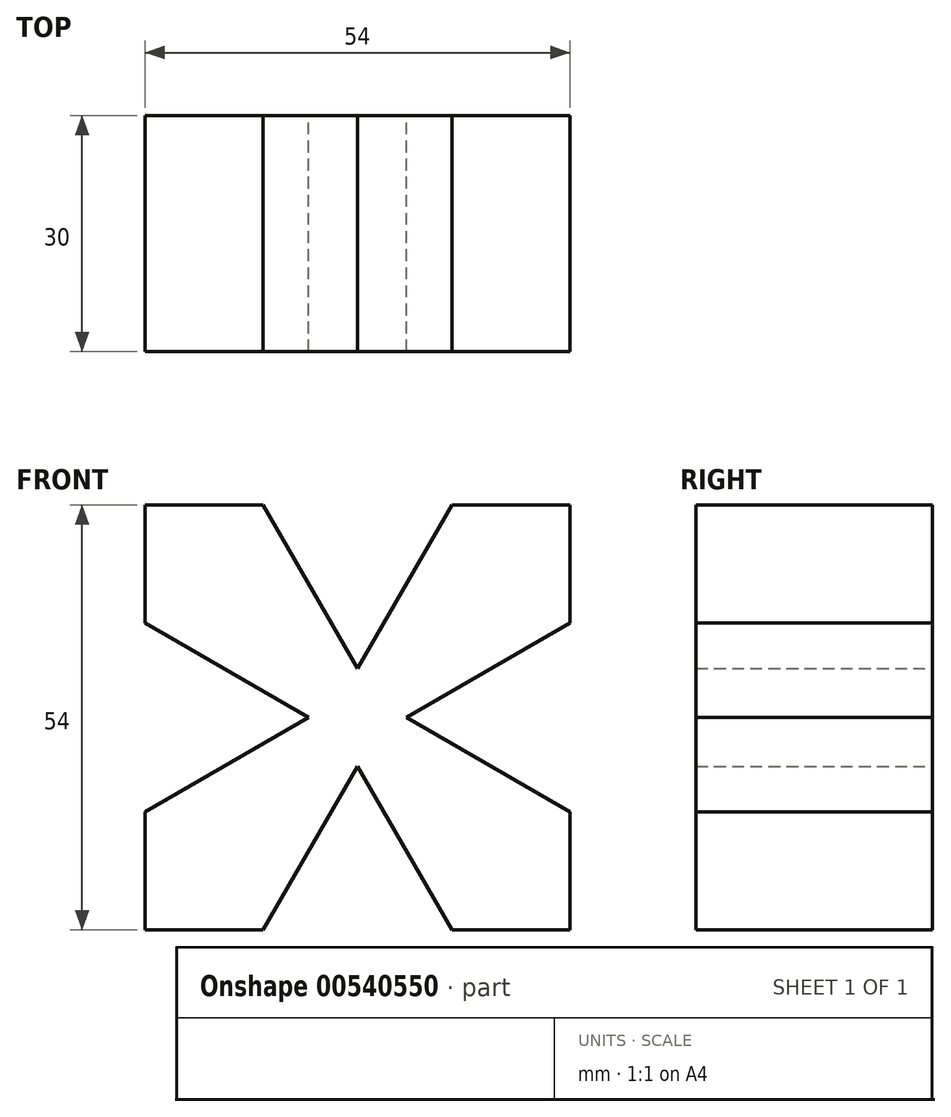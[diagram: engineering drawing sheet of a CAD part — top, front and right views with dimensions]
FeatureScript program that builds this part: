
annotation { "Feature Type Name" : "Feature", "Feature Type Description" : "" }
export const myFeature = defineFeature(function(context is Context, id is Id, definition is map)
    precondition{}
    {
        {
            var Q0;
            Q0=qCreatedBy(makeId("Front.planeOp"),FACE);
            var sketch = newSketch(context, id + "F0", { "sketchPlane" : qUnion([Q0])});
            skLineSegment(sketch, "E0", {"start": v(-71.1, -54.75) * mm, "end": v(-56.1, -54.75) * mm});
            skLineSegment(sketch, "E1", {"start": v(-71.1, -54.75) * mm, "end": v(-71.1, -39.75) * mm});
            skLineSegment(sketch, "E2", {"start": v(-56.1, -54.75) * mm, "end": v(-44.1, -33.97) * mm});
            skLineSegment(sketch, "E3", {"start": v(-71.1, -39.75) * mm, "end": v(-50.3, -27.75) * mm});
            skLineSegment(sketch, "E4", {"start": v(-50.3, -27.75) * mm, "end": v(-71.1, -15.75) * mm});
            skLineSegment(sketch, "E5", {"start": v(-71.1, -15.75) * mm, "end": v(-71.1, -0.75) * mm});
            skLineSegment(sketch, "E6", {"start": v(-71.1, -0.75) * mm, "end": v(-56.1, -0.75) * mm});
            skLineSegment(sketch, "E7", {"start": v(-44.1, -33.97) * mm, "end": v(-32.1, -54.75) * mm});
            skLineSegment(sketch, "E8", {"start": v(-32.1, -54.75) * mm, "end": v(-17.1, -54.75) * mm});
            skLineSegment(sketch, "E9", {"start": v(-17.1, -54.75) * mm, "end": v(-17.1, -39.75) * mm});
            skLineSegment(sketch, "E10", {"start": v(-17.1, -39.75) * mm, "end": v(-37.88, -27.75) * mm});
            skLineSegment(sketch, "E11", {"start": v(-37.88, -27.75) * mm, "end": v(-17.1, -15.75) * mm});
            skLineSegment(sketch, "E12", {"start": v(-17.1, -15.75) * mm, "end": v(-17.1, -0.75) * mm});
            skLineSegment(sketch, "E13", {"start": v(-17.1, -0.75) * mm, "end": v(-32.1, -0.75) * mm});
            skLineSegment(sketch, "E14", {"start": v(-56.1, -0.75) * mm, "end": v(-44.1, -21.53) * mm});
            skLineSegment(sketch, "E15", {"start": v(-44.1, -21.53) * mm, "end": v(-32.1, -0.75) * mm});
            skSolve(sketch);
        }
        {
            var Q0;
            Q0 = qSketchRegion(id + "F0", true);
            extrude(context, id + "F1", {"entities" : qUnion([Q0]), "depth" : 30 * mm, "offsetDistance" : 25 * mm});
        }
    });
